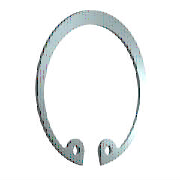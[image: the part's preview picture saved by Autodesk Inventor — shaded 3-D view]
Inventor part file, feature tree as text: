
AUTODESK INVENTOR PART (.ipt)
format: ipt  version: 2025 (Build 290162010, 162A)  size: 163,840 bytes
history: native  units: mm (DEFAULTED — no unit token found)
features: plane x3, other x2, hole x2, sketch x1
ambient origin geometry x8: Origin, YZ Plane, XZ Plane, XY Plane, X Axis, Y Axis, Z Axis, Center Point
bodies: Solid1 (feature_tree)
feature tree (8):
  plane  "WorkPlane1"
  plane  "Work Plane2"
  plane  "WorkPlane2"
  sketch  "Sketch1"  dims[d0=-1.6mm d1=5.2mm d2=26.55mm d3=0.0mm d4=0.0mm d5=4.227778mm d6=23.888889mm d7=0.283333mm d8=1.216667mm d9=3.12mm d10=6.5mm d11=3.12mm d12=6.5mm d13=1.08mm d14=2.25mm d15=1.08mm d16=2.25mm d17=3.66mm d18=23.3mm d19=3.66mm d20=23.3mm d21=6.283185mm d22=6.283185mm d23=6.283185mm d24=6.283185mm d25=1.6mm d26=0.0mm d27=0.0mm d28=0.0mm d29=2.5mm d30=6.0mm d31=4.0mm d32=2.0mm d33=60.0deg d34=8.0mm d35=20.594885mm d36=2.5mm d37=6.0mm d38=4.0mm d39=2.0mm d40=60.0deg d41=8.0mm d42=20.594885mm d47=0.0mm d48=0.0mm d49=0.0mm d50=0.0mm]
  other  "WorkPoint1"
  other  "WorkAxis1"
  hole  "Hole1"  [1 undecoded]
  hole  "Hole2"  [1 undecoded]
note: 2 required parameter values undecoded (feature->parameter linkage not recoverable at this tier; creation-order binding heuristic only, values carry confidence <= 0.55)
